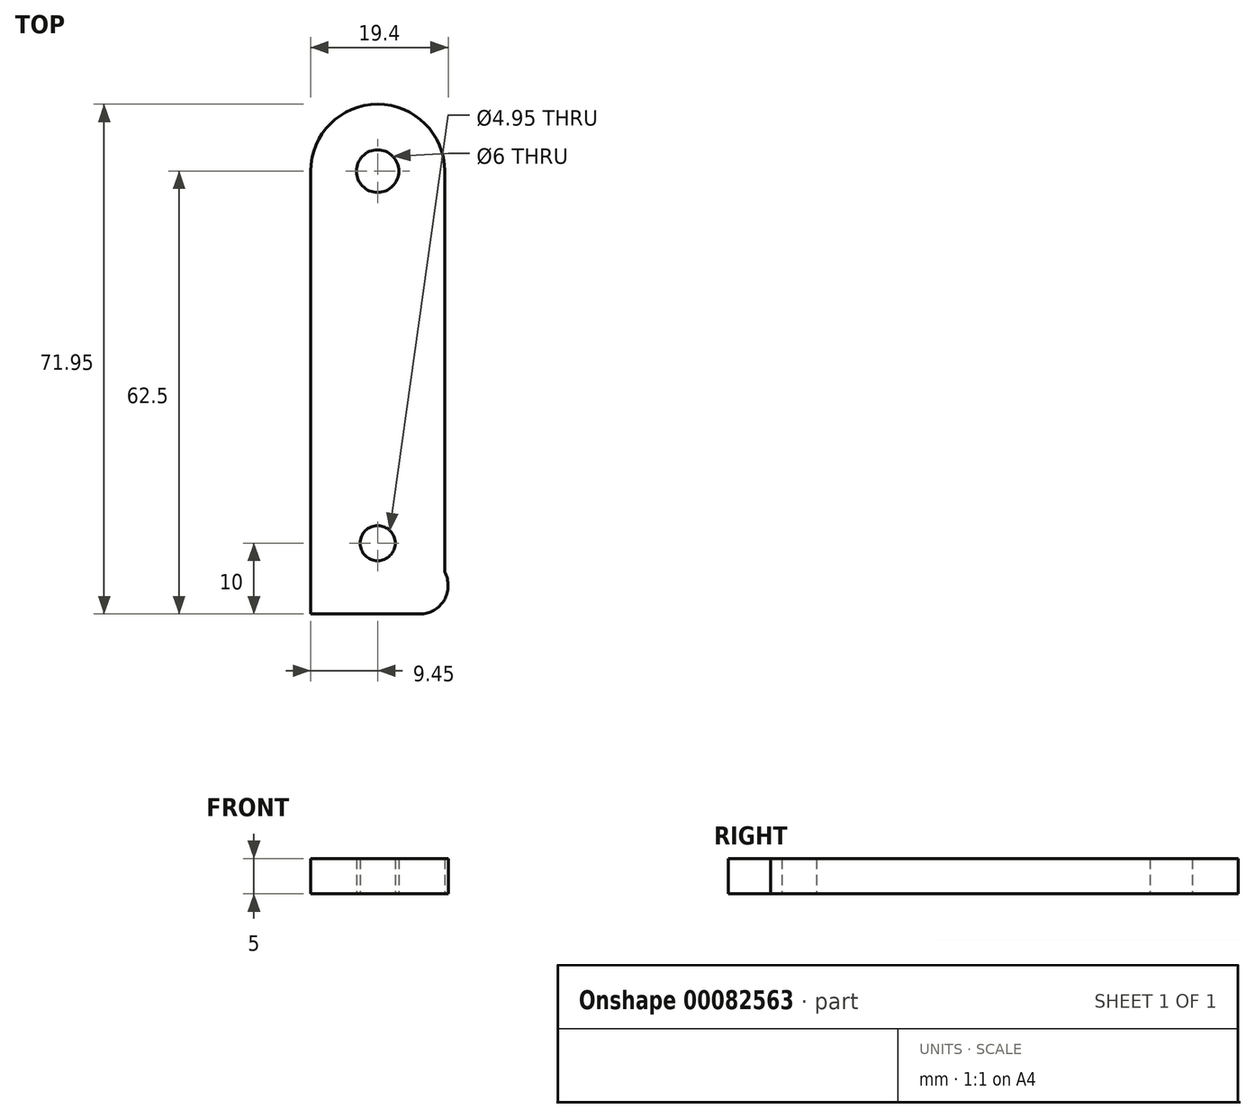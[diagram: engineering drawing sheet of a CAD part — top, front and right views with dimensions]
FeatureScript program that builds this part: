
annotation { "Feature Type Name" : "Feature", "Feature Type Description" : "" }
export const myFeature = defineFeature(function(context is Context, id is Id, definition is map)
    precondition{}
    {
        {
            var Q0;
            Q0=qCreatedBy(makeId("Top.planeOp"),FACE);
            var sketch = newSketch(context, id + "F0", { "sketchPlane" : qUnion([Q0])});
            skLineSegment(sketch, "E0.top", {"start": v(-9.45, -10) * mm, "end": v(5.95, -10) * mm});
            skLineSegment(sketch, "E0.left", {"start": v(-9.45, 52.5) * mm, "end": v(-9.45, -10) * mm});
            skLineSegment(sketch, "E0.right", {"start": v(9.45, 52.5) * mm, "end": v(9.45, -4.06) * mm});
            skCircle(sketch, "E1", {"center": v(0, 0) * mm, "radius": 2.48 * mm});
            skArc(sketch, "E2", {"start": v(9.45, 52.5) * mm, "mid": v(0, 61.95) * mm, "end": v(-9.45, 52.5) * mm});
            skCircle(sketch, "E3", {"center": v(0, 52.5) * mm, "radius": 3 * mm});
            skPoint(sketch, "E4", {"position": v(0, 42.5) * mm});
            skArc(sketch, "E5", {"start": v(5.95, -10) * mm, "mid": v(9.4, -8.03) * mm, "end": v(9.45, -4.06) * mm});
            skPoint(sketch, "E6", {"position": v(9.95, -6) * mm});
            skSolve(sketch);
        }
        {
            var Q0;
            Q0 = qSketchRegion(id + "F0", true);
            extrude(context, id + "F1", {"entities" : qUnion([Q0]), "depth" : 5 * mm});
        }
    });
